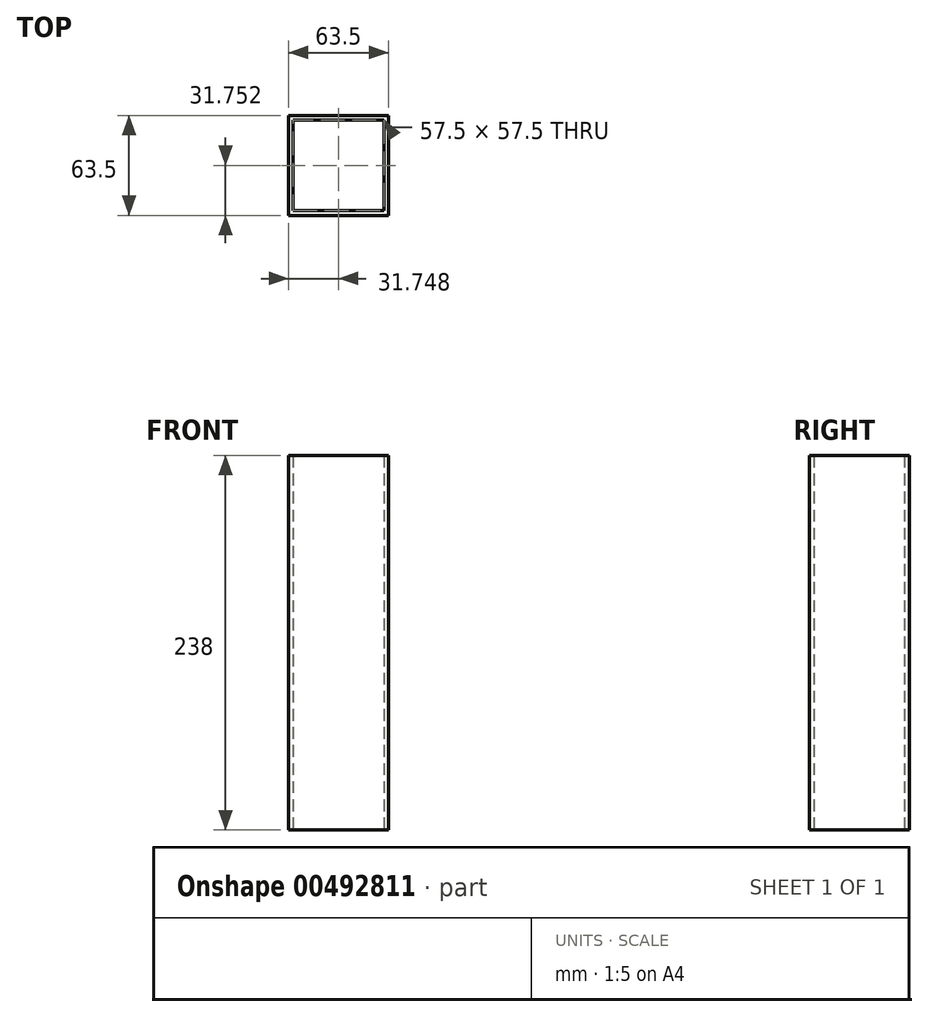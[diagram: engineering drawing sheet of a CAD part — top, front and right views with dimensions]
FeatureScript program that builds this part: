
annotation { "Feature Type Name" : "Feature", "Feature Type Description" : "" }
export const myFeature = defineFeature(function(context is Context, id is Id, definition is map)
    precondition{}
    {
        {
            var Q0;
            Q0=qCreatedBy(makeId("Top.planeOp"),FACE);
            var sketch = newSketch(context, id + "F0", { "sketchPlane" : qUnion([Q0])});
            skLineSegment(sketch, "E0.bottom", {"start": v(-30.17, 28.05) * mm, "end": v(27.33, 28.05) * mm});
            skLineSegment(sketch, "E0.top", {"start": v(-30.17, -29.45) * mm, "end": v(27.33, -29.45) * mm});
            skLineSegment(sketch, "E0.left", {"start": v(-30.17, 28.05) * mm, "end": v(-30.17, -29.45) * mm});
            skLineSegment(sketch, "E0.right", {"start": v(27.33, 28.05) * mm, "end": v(27.33, -29.45) * mm});
            skLineSegment(sketch, "E1.bottom", {"start": v(-33.17, 31.05) * mm, "end": v(30.33, 31.05) * mm});
            skLineSegment(sketch, "E1.top", {"start": v(-33.17, -32.45) * mm, "end": v(30.33, -32.45) * mm});
            skLineSegment(sketch, "E1.left", {"start": v(-33.17, 31.05) * mm, "end": v(-33.17, -32.45) * mm});
            skLineSegment(sketch, "E1.right", {"start": v(30.33, 31.05) * mm, "end": v(30.33, -32.45) * mm});
            skSolve(sketch);
        }
        {
            var Q0;
            Q0 = qSketchRegion(id + "F0", true);
            extrude(context, id + "F1", {"entities" : qUnion([Q0]), "depth" : 238 * mm});
        }
    });
